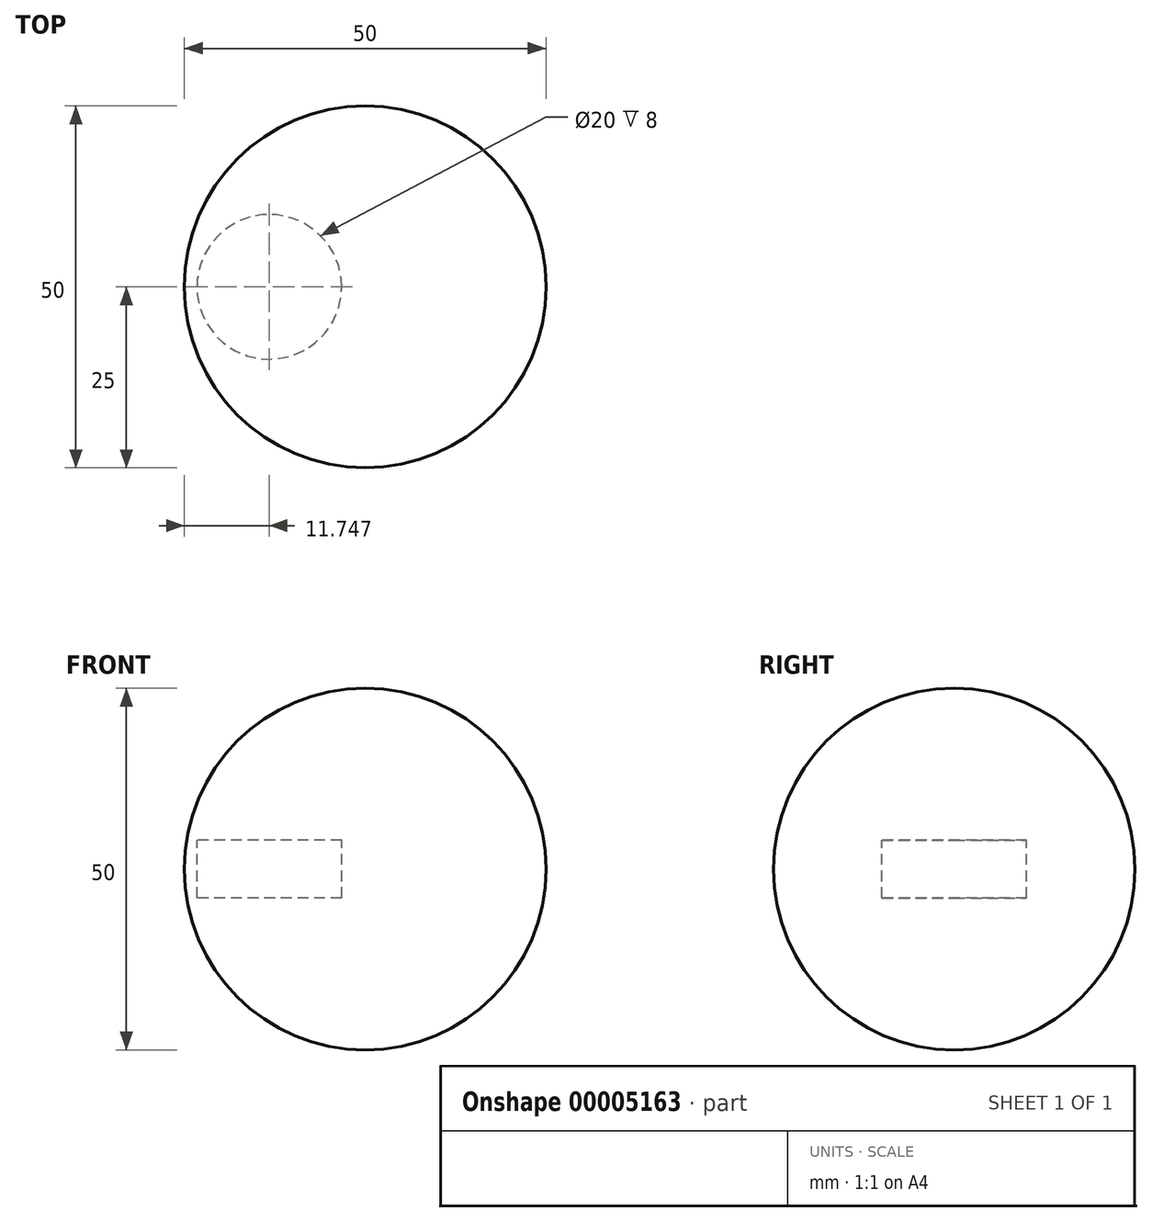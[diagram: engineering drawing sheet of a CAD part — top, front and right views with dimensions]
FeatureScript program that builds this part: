
annotation { "Feature Type Name" : "Feature", "Feature Type Description" : "" }
export const myFeature = defineFeature(function(context is Context, id is Id, definition is map)
    precondition{}
    {
        {
            var Q0;
            Q0=qCreatedBy(makeId("Top.planeOp"),FACE);
            var sketch = newSketch(context, id + "F0", { "sketchPlane" : qUnion([Q0])});
            skCircle(sketch, "E0", {"center": v(0, 0) * mm, "radius": 25 * mm});
            skLineSegment(sketch, "E1", {"start": v(-25, 0) * mm, "end": v(25, 0) * mm});
            skSolve(sketch);
        }
        {
            var Q0;
            {var subQ0=sQuery(id+"F0.wireOp",EDGE,"E1");Q0=makeQuery(id+"F0.imprint","IMPRINT",FACE,{"disambiguationData":[TD([[makeQuery(id+"F0.imprint","IMPRINT",EDGE,{"derivedFrom":subQ0}),1.0]])]});}
            var Q1;
            Q1=sQuery(id+"F0.wireOp",EDGE,"E1");
            revolve(context, id + "F1", {"entities" : qUnion([Q0]), "axis" : qUnion([Q1]), "revolveType" : RevolveType.FULL});
        }
        {
            var Q0;
            Q0=qCreatedBy(makeId("Top.planeOp"),FACE);
            var sketch = newSketch(context, id + "F2", { "sketchPlane" : qUnion([Q0])});
            skCircle(sketch, "E2", {"center": v(-13.25, 0) * mm, "radius": 10 * mm});
            skLineSegment(sketch, "E3", {"start": v(-13.25, -10) * mm, "end": v(-13.25, 10) * mm});
            skPoint(sketch, "E4", {"position": v(0, 0) * mm});
            skSolve(sketch);
        }
        {
            var Q0;
            {var subQ0=sQuery(id+"F2.wireOp",EDGE,"E3");Q0=makeQuery(id+"F2.imprint","IMPRINT",FACE,{"disambiguationData":[TD([[makeQuery(id+"F2.imprint","IMPRINT",EDGE,{"derivedFrom":subQ0}),1.0]])]});}
            var Q1;
            {var subQ0=sQuery(id+"F2.wireOp",EDGE,"E3");Q1=makeQuery(id+"F2.imprint","IMPRINT",FACE,{"disambiguationData":[TD([[makeQuery(id+"F2.imprint","IMPRINT",EDGE,{"derivedFrom":subQ0}),-1.0]])]});}
            extrude(context, id + "F3", {"entities" : qUnion([Q0, Q1]), "operationType" : NewBodyOperationType.REMOVE, "oppositeDirection" : true, "depth" : 4 * mm});
        }
        {
            var Q0;
            {var subQ0=sQuery(id+"F2.wireOp",EDGE,"E3");Q0=makeQuery(id+"F2.imprint","IMPRINT",FACE,{"disambiguationData":[TD([[makeQuery(id+"F2.imprint","IMPRINT",EDGE,{"derivedFrom":subQ0}),1.0]])]});}
            var Q1;
            {var subQ0=sQuery(id+"F2.wireOp",EDGE,"E3");Q1=makeQuery(id+"F2.imprint","IMPRINT",FACE,{"disambiguationData":[TD([[makeQuery(id+"F2.imprint","IMPRINT",EDGE,{"derivedFrom":subQ0}),-1.0]])]});}
            extrude(context, id + "F4", {"entities" : qUnion([Q0, Q1]), "operationType" : NewBodyOperationType.REMOVE, "depth" : 4 * mm});
        }
        {
            var Q0;
            Q0=makeQuery(id+"F1.opRevolve","SWEPT_BODY",BODY,{"disambiguationData":[OSD([sQuery(id+"F0.wireOp",EDGE,"E0"),sQuery(id+"F0.wireOp",EDGE,"E1")])]});
            transform(context, id + "F5", {"entities" : qUnion([Q0]), "transformType" : TransformType.TRANSLATION_3D, "dx" : 0 * mm, "dy" : 0 * mm, "dz" : 25 * mm, "makeCopy" : false});
        }
        {
            var Q0;
            Q0=qCreatedBy(makeId("Top.planeOp"),FACE);
            var sketch = newSketch(context, id + "F6", { "sketchPlane" : qUnion([Q0])});
            skCircle(sketch, "E5", {"center": v(0, 0) * mm, "radius": 12.22 * mm});
            skSolve(sketch);
        }
        {
            var Q0;
            Q0=makeQuery(id+"F1.opRevolve","SWEPT_BODY",BODY,{"disambiguationData":[OSD([sQuery(id+"F0.wireOp",EDGE,"E0"),sQuery(id+"F0.wireOp",EDGE,"E1")])]});
            transform(context, id + "F7", {"entities" : qUnion([Q0]), "transformType" : TransformType.TRANSLATION_3D, "dx" : 50 * mm, "dy" : 50 * mm, "dz" : 0 * mm, "makeCopy" : false});
        }
    });
